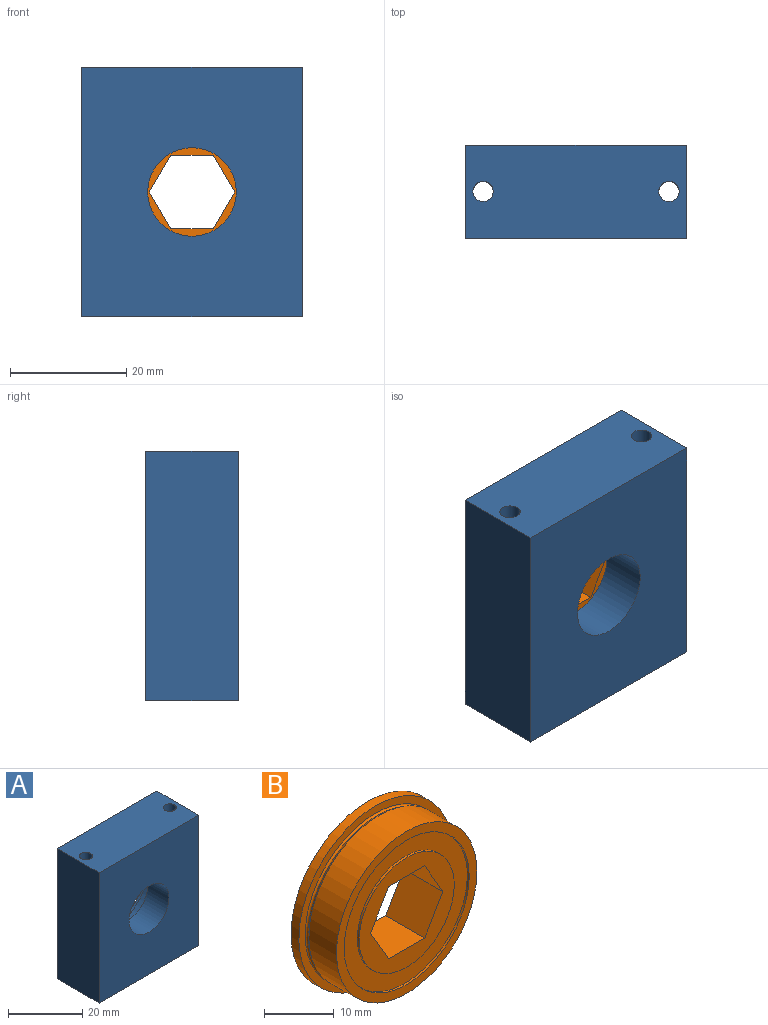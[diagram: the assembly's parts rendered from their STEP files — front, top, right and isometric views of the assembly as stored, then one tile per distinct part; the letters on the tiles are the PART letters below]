
ASSEMBLY  parts=2 mates=1
PART A: 13 faces, bbox 38x16x43 mm
  f0: plane 38x16mm, normal (0,0,1), area 588.8mm2, adj f1,f4,f5,f10,f11,f12
  f1: plane 43x16mm, normal (1,0,0), area 688mm2, adj f0,f2,f5,f10
  f2: plane 38x16mm, normal (0,0,-1), area 588.8mm2, adj f1,f4,f5,f10,f11,f12
  f3: cylinder r=15.56mm len=31.12mm, axis (0,1,0), area 155.2mm2, adj f5,f6
  f4: plane 43x16mm, normal (-1,0,0), area 688mm2, adj f0,f2,f5,f10
  f5: plane 43x38mm, normal (0,1,0), area 873.6mm2, adj f0,f1,f2,f3,f4
  f6: plane 31.12x31.12mm, normal (0,1,0), area 120.2mm2, adj f3,f7
  f7: cylinder r=14.27mm len=28.55mm, axis (0,1,0), area 568.8mm2, adj f6,f8,f11,f12
  f8: plane 28.55x28.5mm, normal (0,1,0), area 457.7mm2, adj f7,f9,f11,f12
  f9: cylinder r=7.62mm len=15.24mm, axis (0,1,0), area 386mm2, adj f8,f10
  f10: plane 43x38mm, normal (0,-1,0), area 1451.6mm2, adj f0,f1,f2,f4,f9
  f11: cylinder r=1.75mm len=43mm, axis (0,0,1), area 472.4mm2, adj f0,f2,f7,f8
  f12: cylinder r=1.75mm len=43mm, axis (0,0,1), area 472.4mm2, adj f0,f2,f7,f8
PART B: 21 faces, bbox 31.1x7.9x31.1 mm
  f0: torus R=14.27mm, axis (0,1,0), area 46.4mm2, adj f4,f10
  f1: cylinder r=9.65mm len=19.3mm, axis (0,1,0), area 23.1mm2, adj f12,f13
  f2: cylinder r=12.7mm len=25.4mm, axis (0,1,0), area 30.4mm2, adj f11,f12
  f3: cylinder r=14.27mm len=28.55mm, axis (0,1,0), area 502.3mm2, adj f4,f11
  f4: cone r=14.06mm half-angle=30deg, axis (0,-1,0), area 38.5mm2, adj f0,f3
  f5: cylinder r=15.56mm len=31.12mm, axis (0,1,0), area 155.2mm2, adj f9,f10
  f6: cylinder r=12.7mm len=25.4mm, axis (0,1,0), area 30.4mm2, adj f8,f9
  f7: cylinder r=9.65mm len=19.3mm, axis (0,1,0), area 23.1mm2, adj f8,f14
  f8: plane 25.4x25.4mm, normal (0,1,0), area 214mm2, adj f6,f7
  f9: plane 31.12x31.12mm, normal (0,1,0), area 253.7mm2, adj f5,f6
  f10: plane 31.12x31.12mm, normal (0,-1,0), area 120.2mm2, adj f0,f5
  f11: plane 28.55x28.55mm, normal (0,-1,0), area 133.5mm2, adj f2,f3
  f12: plane 25.4x25.4mm, normal (0,-1,0), area 214mm2, adj f1,f2
  f13: plane 19.3x19.3mm, normal (0,-1,0), area 152.6mm2, adj f1,f15,f16,f17,f18,f19,f20
  f14: plane 19.3x19.3mm, normal (0,1,0), area 152.6mm2, adj f7,f15,f16,f17,f18,f19,f20
  f15: plane 7.94x6.36mm, normal (-0.87,0,0.5), area 58.3mm2, adj f13,f14,f16,f20
  f16: plane 7.94x6.36mm, normal (-0.87,0,-0.5), area 58.3mm2, adj f13,f14,f15,f17
  f17: plane 7.94x7.34mm, normal (0,0,-1), area 58.3mm2, adj f13,f14,f16,f18
  f18: plane 7.94x6.36mm, normal (0.87,0,-0.5), area 58.3mm2, adj f13,f14,f17,f19
  f19: plane 7.94x6.36mm, normal (0.87,0,0.5), area 58.3mm2, adj f13,f14,f18,f20
  f20: plane 7.94x7.34mm, normal (0,0,1), area 58.3mm2, adj f13,f14,f15,f19
PLACE A at identity
PLACE B at identity
MATE revolute A.f3 <-> B.f0  axis (0,1,0) through (0,6.35,0)mm
